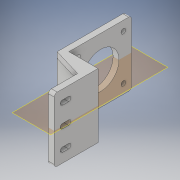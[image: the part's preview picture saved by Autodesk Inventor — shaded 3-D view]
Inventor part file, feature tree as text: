
AUTODESK INVENTOR PART (.ipt)
format: ipt  version: 2018 (Build 220112000, 112)  size: 177,152 bytes
history: native  units: in
note: dims shown in document units (in); Inventor stores cm internally (conversion verified against a paired STEP export)
features: extrude x4, sketch x4, fillet x1, projected_geometry x1
ambient origin geometry x8: Origin, YZ Plane, XZ Plane, XY Plane, X Axis, Y Axis, Z Axis, Center Point
bodies: Solid1 (feature_tree)
feature tree (10):
  extrude  "Extrusion1"  Depth=1.6929in
  extrude  "Extrusion2"  Depth=0.1575in
  extrude  "Extrusion3"  Depth=0.7874in
  extrude  "Extrusion4"  Depth=1.7323in TaperAngle=0.0deg
  fillet  "Fillet1"  Radius=0.126in
  sketch  "Sketch1"  dims[d0=0.7874in d1=1.6929in]
  sketch  "Sketch2"  dims[d2=0.1575in d3=0.1575in]
  projected_geometry  "Projected Loop1"
  sketch  "Sketch3"  dims[d4=1.1811in d5=0.7874in]
  sketch  "Sketch4"  dims[d6=0.1575in d7=1.7323in d8=0.0in d9=0.126in d10=0.9843in d11=0.8327in d12=1.2205in d13=1.2205in d14=0.6102in d15=0.6102in d16=1.7323in d17=0.0in d18=0.126in d19=0.1575in d20=0.315in d21=0.315in d22=1.7323in d23=0.0in d24=1.7323in d25=0.0in d26=0.1575in d27=0.1575in d28=0.0787in]
